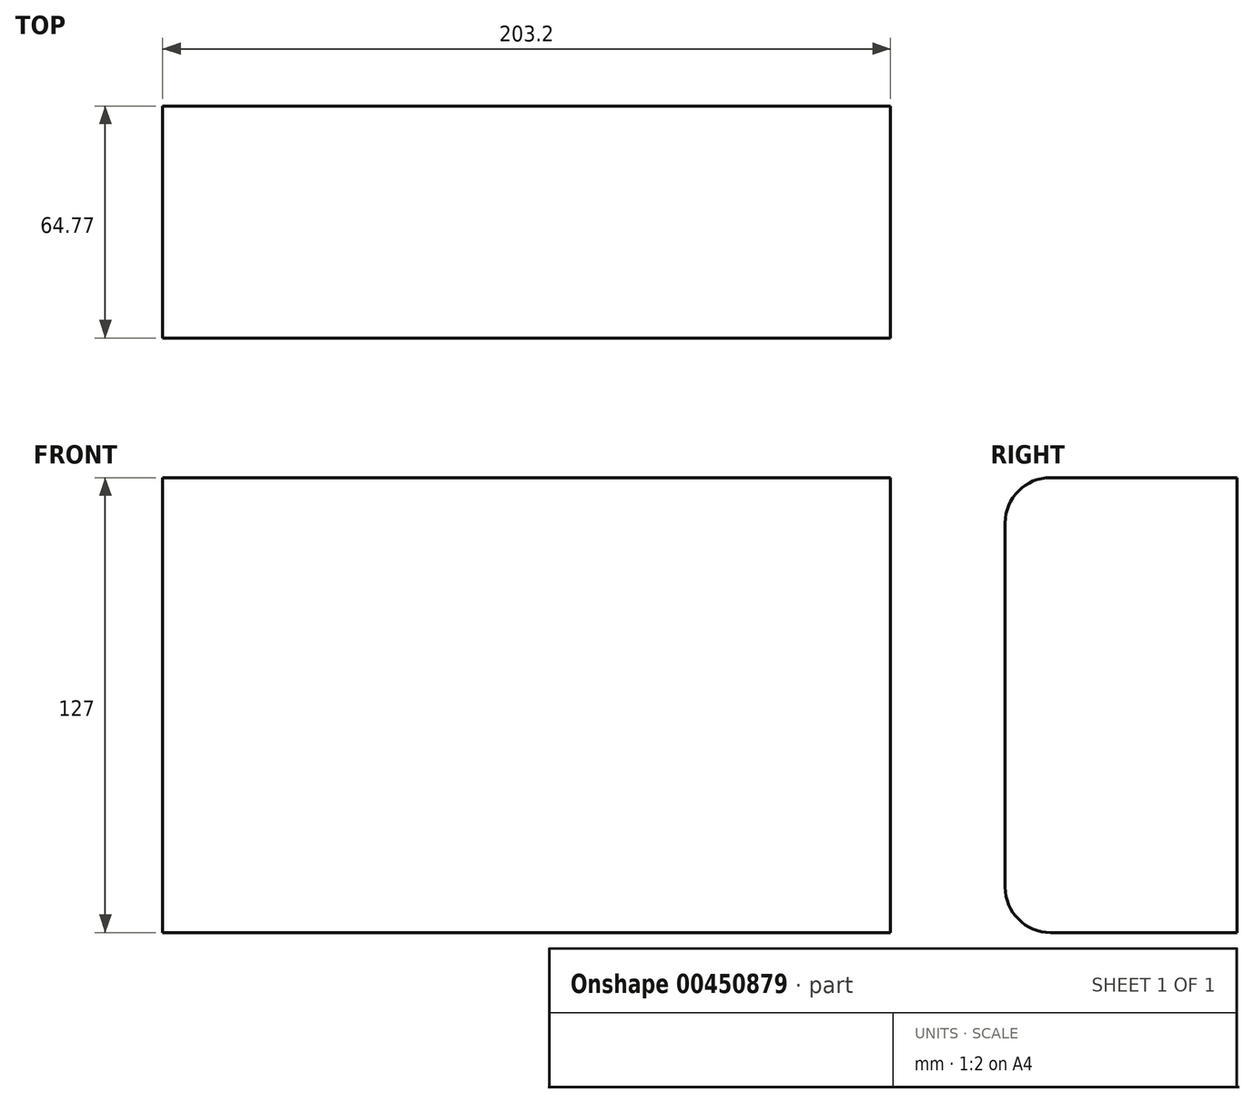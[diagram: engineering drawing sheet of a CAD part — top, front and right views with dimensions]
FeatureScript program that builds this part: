
annotation { "Feature Type Name" : "Feature", "Feature Type Description" : "" }
export const myFeature = defineFeature(function(context is Context, id is Id, definition is map)
    precondition{}
    {
        {
            var Q0;
            Q0=qCreatedBy(makeId("Right.planeOp"),FACE);
            var sketch = newSketch(context, id + "F0", { "sketchPlane" : qUnion([Q0])});
            skLineSegment(sketch, "E0.bottom", {"start": v(0, 63.5) * mm, "end": v(-19.05, 63.5) * mm});
            skLineSegment(sketch, "E0.top", {"start": v(0, -63.5) * mm, "end": v(-19.05, -63.5) * mm});
            skLineSegment(sketch, "E0.left", {"start": v(0, 63.5) * mm, "end": v(0, -63.5) * mm});
            skLineSegment(sketch, "E0.right", {"start": v(-19.05, 63.5) * mm, "end": v(-19.05, -63.5) * mm});
            skLineSegment(sketch, "E1.bottom", {"start": v(-19.05, 63.5) * mm, "end": v(-71.12, 63.5) * mm});
            skLineSegment(sketch, "E1.top", {"start": v(-19.05, -63.5) * mm, "end": v(-71.12, -63.5) * mm});
            skLineSegment(sketch, "E1.right", {"start": v(-83.82, 50.8) * mm, "end": v(-83.82, -50.8) * mm});
            skPoint(sketch, "E2.visualSharp", {"position": v(-83.82, 63.5) * mm});
            skArc(sketch, "E2.filletArc", {"start": v(-71.12, 63.5) * mm, "mid": v(-80.1, 59.78) * mm, "end": v(-83.82, 50.8) * mm});
            skPoint(sketch, "E3.visualSharp", {"position": v(-83.82, -63.5) * mm});
            skArc(sketch, "E3.filletArc", {"start": v(-83.82, -50.8) * mm, "mid": v(-80.1, -59.78) * mm, "end": v(-71.12, -63.5) * mm});
            skSolve(sketch);
        }
        {
            var Q0;
            Q0=makeQuery(id+"F0.imprint","IMPRINT",FACE,{"disambiguationData":[TD([[makeQuery(id+"F0.imprint","IMPRINT",EDGE,{"derivedFrom":sQuery(id+"F0.wireOp",EDGE,"E1.bottom")}),1.0]])]});
            extrude(context, id + "F1", {"entities" : qUnion([Q0]), "depth" : 203.2 * mm});
        }
    });
